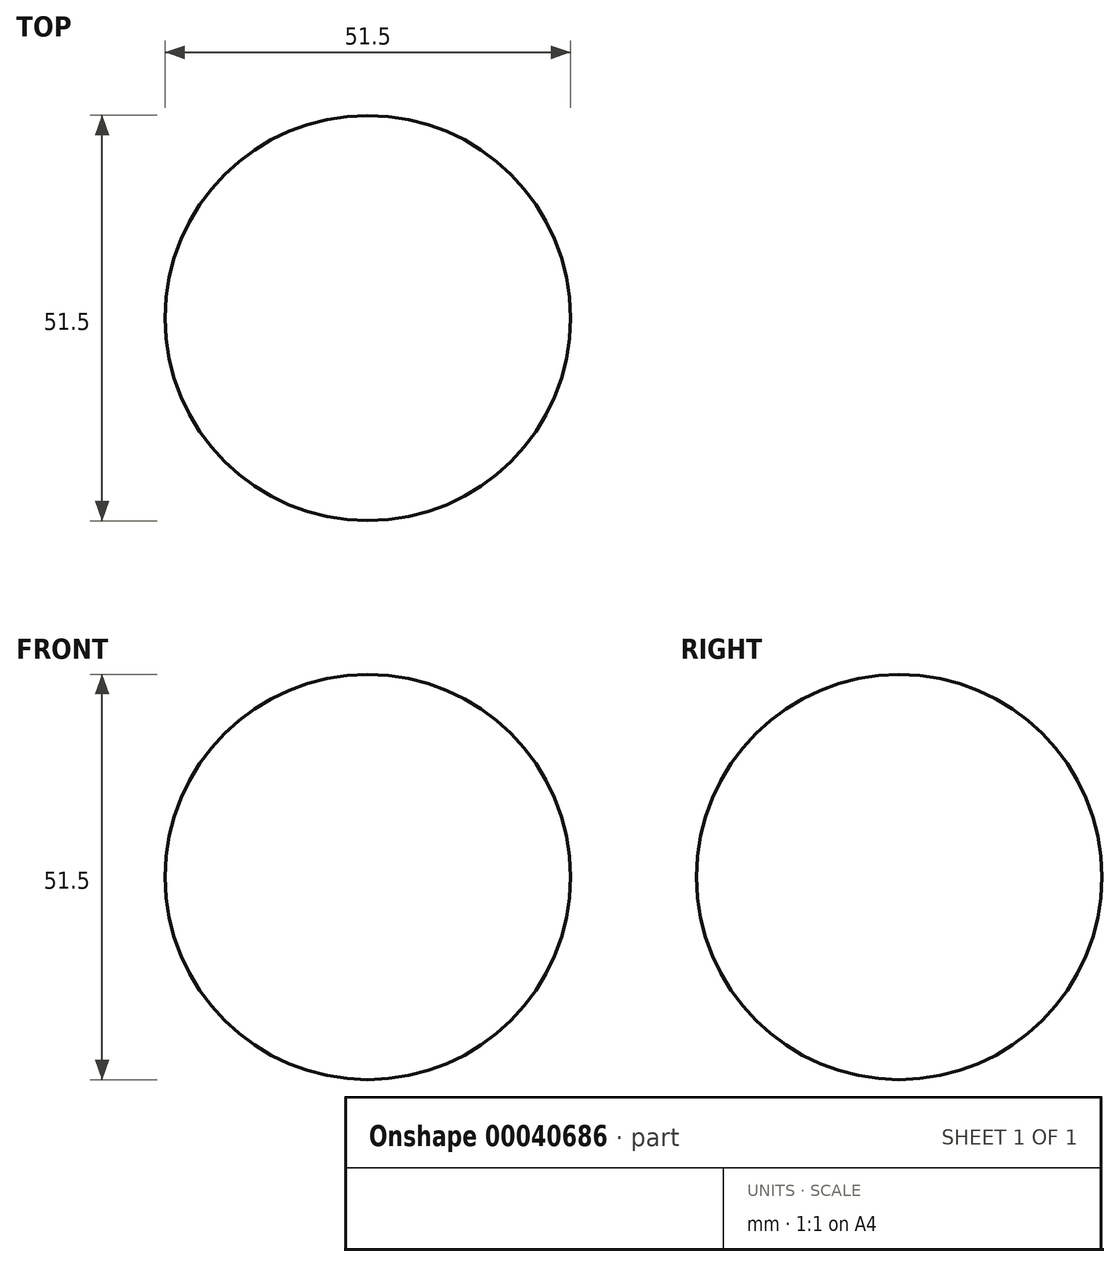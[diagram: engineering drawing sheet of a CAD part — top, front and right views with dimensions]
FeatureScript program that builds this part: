
annotation { "Feature Type Name" : "Feature", "Feature Type Description" : "" }
export const myFeature = defineFeature(function(context is Context, id is Id, definition is map)
    precondition{}
    {
        {
            var Q0;
            Q0=qCreatedBy(makeId("Right.planeOp"),FACE);
            var sketch = newSketch(context, id + "F0", { "sketchPlane" : qUnion([Q0])});
            skArc(sketch, "E0", {"start": v(-25.75, 0) * mm, "mid": v(0, 25.75) * mm, "end": v(25.75, 0) * mm});
            skLineSegment(sketch, "E1", {"start": v(35.61, 0) * mm, "end": v(-47.33, 0) * mm, "construction": true});
            skSolve(sketch);
        }
        {
            var Q0;
            Q0=sQuery(id+"F0.wireOp",EDGE,"E0");
            var Q1;
            Q1=sQuery(id+"F0.wireOp",EDGE,"E1");
            revolve(context, id + "F1", {"bodyType" : ToolBodyType.SURFACE, "surfaceEntities" : qUnion([Q0]), "axis" : qUnion([Q1]), "revolveType" : RevolveType.FULL});
        }
    });
